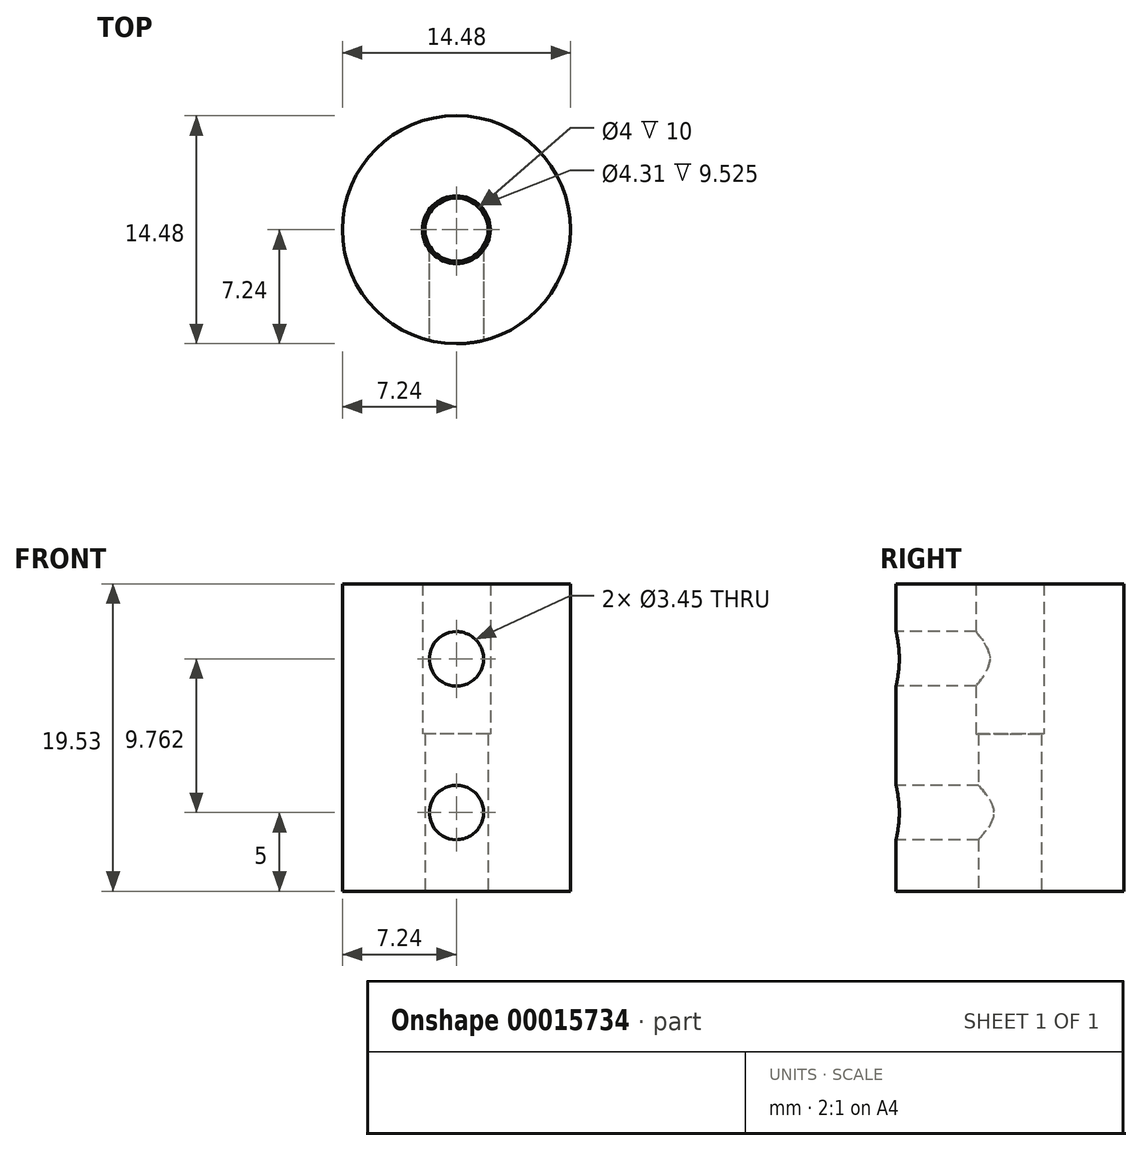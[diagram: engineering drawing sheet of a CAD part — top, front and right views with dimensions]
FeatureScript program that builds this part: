
annotation { "Feature Type Name" : "Feature", "Feature Type Description" : "" }
export const myFeature = defineFeature(function(context is Context, id is Id, definition is map)
    precondition{}
    {
        {
            var Q0;
            Q0=qCreatedBy(makeId("Top.planeOp"),FACE);
            var sketch = newSketch(context, id + "F0", { "sketchPlane" : qUnion([Q0])});
            skLineSegment(sketch, "E0.bottom", {"start": v(7.24, -7.24) * mm, "end": v(-7.24, -7.24) * mm});
            skLineSegment(sketch, "E0.top", {"start": v(7.24, 7.24) * mm, "end": v(-7.24, 7.24) * mm});
            skLineSegment(sketch, "E0.left", {"start": v(7.24, -7.24) * mm, "end": v(7.24, 7.24) * mm});
            skLineSegment(sketch, "E0.right", {"start": v(-7.24, -7.24) * mm, "end": v(-7.24, 7.24) * mm});
            skPoint(sketch, "E0.middle", {"position": v(0, 0) * mm});
            skCircle(sketch, "E1", {"center": v(0, 0) * mm, "radius": 7.24 * mm, "construction": true});
            skCircle(sketch, "E2", {"center": v(0, 0) * mm, "radius": 2.15 * mm, "construction": true});
            skLineSegment(sketch, "E3", {"start": v(0, 0) * mm, "end": v(2.15, 0) * mm, "construction": true});
            skLineSegment(sketch, "E4.bottom", {"start": v(2.15, 2.15) * mm, "end": v(6.92, 2.15) * mm, "construction": true});
            skLineSegment(sketch, "E4.top", {"start": v(2.15, -2.15) * mm, "end": v(6.92, -2.15) * mm, "construction": true});
            skLineSegment(sketch, "E4.left", {"start": v(2.15, 2.15) * mm, "end": v(2.15, -2.15) * mm, "construction": true});
            skLineSegment(sketch, "E4.right", {"start": v(6.92, 2.15) * mm, "end": v(6.92, -2.15) * mm, "construction": true});
            skCircle(sketch, "E5", {"center": v(0, 0) * mm, "radius": 2 * mm});
            skSolve(sketch);
        }
        {
            var Q0;
            Q0 = qSketchRegion(id + "F0", true);
            extrude(context, id + "F1", {"entities" : qUnion([Q0]), "depth" : 10 * mm});
        }
        {
            var Q0;
            Q0=makeQuery(id+"F1.opExtrude","CAP_FACE",FACE,{"disambiguationData":[OSD([sQuery(id+"F0.wireOp",EDGE,"E0.bottom"),sQuery(id+"F0.wireOp",EDGE,"E0.top"),sQuery(id+"F0.wireOp",EDGE,"E0.left"),sQuery(id+"F0.wireOp",EDGE,"E0.right"),sQuery(id+"F0.wireOp",EDGE,"E5")])],"isStart":false});
            var sketch = newSketch(context, id + "F2", { "sketchPlane" : qUnion([Q0])});
            skLineSegment(sketch, "E6.bottom", {"start": v(-7.24, 7.24) * mm, "end": v(7.24, 7.24) * mm});
            skLineSegment(sketch, "E6.top", {"start": v(-7.24, -7.24) * mm, "end": v(7.24, -7.24) * mm});
            skLineSegment(sketch, "E6.left", {"start": v(-7.24, 7.24) * mm, "end": v(-7.24, -7.24) * mm});
            skLineSegment(sketch, "E6.right", {"start": v(7.24, 7.24) * mm, "end": v(7.24, -7.24) * mm});
            skCircle(sketch, "E7", {"center": v(0, 0) * mm, "radius": 2.15 * mm});
            skSolve(sketch);
        }
        {
            var Q0;
            Q0 = qSketchRegion(id + "F2", true);
            extrude(context, id + "F3", {"entities" : qUnion([Q0]), "operationType" : NewBodyOperationType.ADD, "depth" : 9.52 * mm});
        }
        {
            var Q0;
            Q0=makeQuery(id+"F3.boolean.opBoolean","MERGE",FACE,{"derivedFrom":[makeQuery(id+"F1.opExtrude","SWEPT_FACE",FACE,{"disambiguationData":[OSD([sQuery(id+"F0.wireOp",EDGE,"E0.bottom")])]}),makeQuery(id+"F3.opExtrude","SWEPT_FACE",FACE,{"disambiguationData":[OSD([sQuery(id+"F2.wireOp",EDGE,"E6.top")])]})]});
            var sketch = newSketch(context, id + "F4", { "sketchPlane" : qUnion([Q0])});
            skLineSegment(sketch, "E8", {"start": v(0, 19.53) * mm, "end": v(0, 10) * mm, "construction": true});
            skLineSegment(sketch, "E9", {"start": v(0, 10) * mm, "end": v(0, 0) * mm, "construction": true});
            skCircle(sketch, "E10", {"center": v(0, 14.76) * mm, "radius": 1.73 * mm});
            skCircle(sketch, "E11", {"center": v(0, 5) * mm, "radius": 1.73 * mm});
            skSolve(sketch);
        }
        {
            var Q0;
            Q0 = qSketchRegion(id + "F4", true);
            var Q1;
            Q1=makeQuery(id+"F1.opExtrude","SWEPT_FACE",FACE,{"disambiguationData":[OSD([sQuery(id+"F0.wireOp",EDGE,"E5")])]});
            extrude(context, id + "F5", {"entities" : qUnion([Q0]), "operationType" : NewBodyOperationType.REMOVE, "endBound" : BoundingType.UP_TO_SURFACE, "oppositeDirection" : true, "endBoundEntityFace" : qUnion([Q1]), "depth" : 25.4 * mm});
        }
        {
            var Q0;
            Q0=makeQuery(id+"F3.boolean.opBoolean","MERGE",EDGE,{"derivedFrom":[makeQuery(id+"F1.opExtrude","SWEPT_EDGE",EDGE,{"disambiguationData":[OSD([sQuery(id+"F0.wireOp",EDGE,"E0.bottom"),sQuery(id+"F0.wireOp",EDGE,"E0.left")])]}),makeQuery(id+"F3.opExtrude","SWEPT_EDGE",EDGE,{"disambiguationData":[OSD([sQuery(id+"F2.wireOp",EDGE,"E6.top"),sQuery(id+"F2.wireOp",EDGE,"E6.right")])]})]});
            var Q1;
            Q1=makeQuery(id+"F3.boolean.opBoolean","MERGE",EDGE,{"derivedFrom":[makeQuery(id+"F1.opExtrude","SWEPT_EDGE",EDGE,{"disambiguationData":[OSD([sQuery(id+"F0.wireOp",EDGE,"E0.top"),sQuery(id+"F0.wireOp",EDGE,"E0.left")])]}),makeQuery(id+"F3.opExtrude","SWEPT_EDGE",EDGE,{"disambiguationData":[OSD([sQuery(id+"F2.wireOp",EDGE,"E6.bottom"),sQuery(id+"F2.wireOp",EDGE,"E6.right")])]})]});
            var Q2;
            Q2=makeQuery(id+"F3.boolean.opBoolean","MERGE",EDGE,{"derivedFrom":[makeQuery(id+"F1.opExtrude","SWEPT_EDGE",EDGE,{"disambiguationData":[OSD([sQuery(id+"F0.wireOp",EDGE,"E0.bottom"),sQuery(id+"F0.wireOp",EDGE,"E0.right")])]}),makeQuery(id+"F3.opExtrude","SWEPT_EDGE",EDGE,{"disambiguationData":[OSD([sQuery(id+"F2.wireOp",EDGE,"E6.top"),sQuery(id+"F2.wireOp",EDGE,"E6.left")])]})]});
            var Q3;
            Q3=makeQuery(id+"F3.boolean.opBoolean","MERGE",EDGE,{"derivedFrom":[makeQuery(id+"F1.opExtrude","SWEPT_EDGE",EDGE,{"disambiguationData":[OSD([sQuery(id+"F0.wireOp",EDGE,"E0.top"),sQuery(id+"F0.wireOp",EDGE,"E0.right")])]}),makeQuery(id+"F3.opExtrude","SWEPT_EDGE",EDGE,{"disambiguationData":[OSD([sQuery(id+"F2.wireOp",EDGE,"E6.bottom"),sQuery(id+"F2.wireOp",EDGE,"E6.left")])]})]});
            fillet(context, id + "F6", {"entities" : qUnion([Q0, Q1, Q2, Q3]), "radius" : 7.24 * mm, "tangentPropagation" : true, "allowEdgeOverflow" : false});
        }
    });
